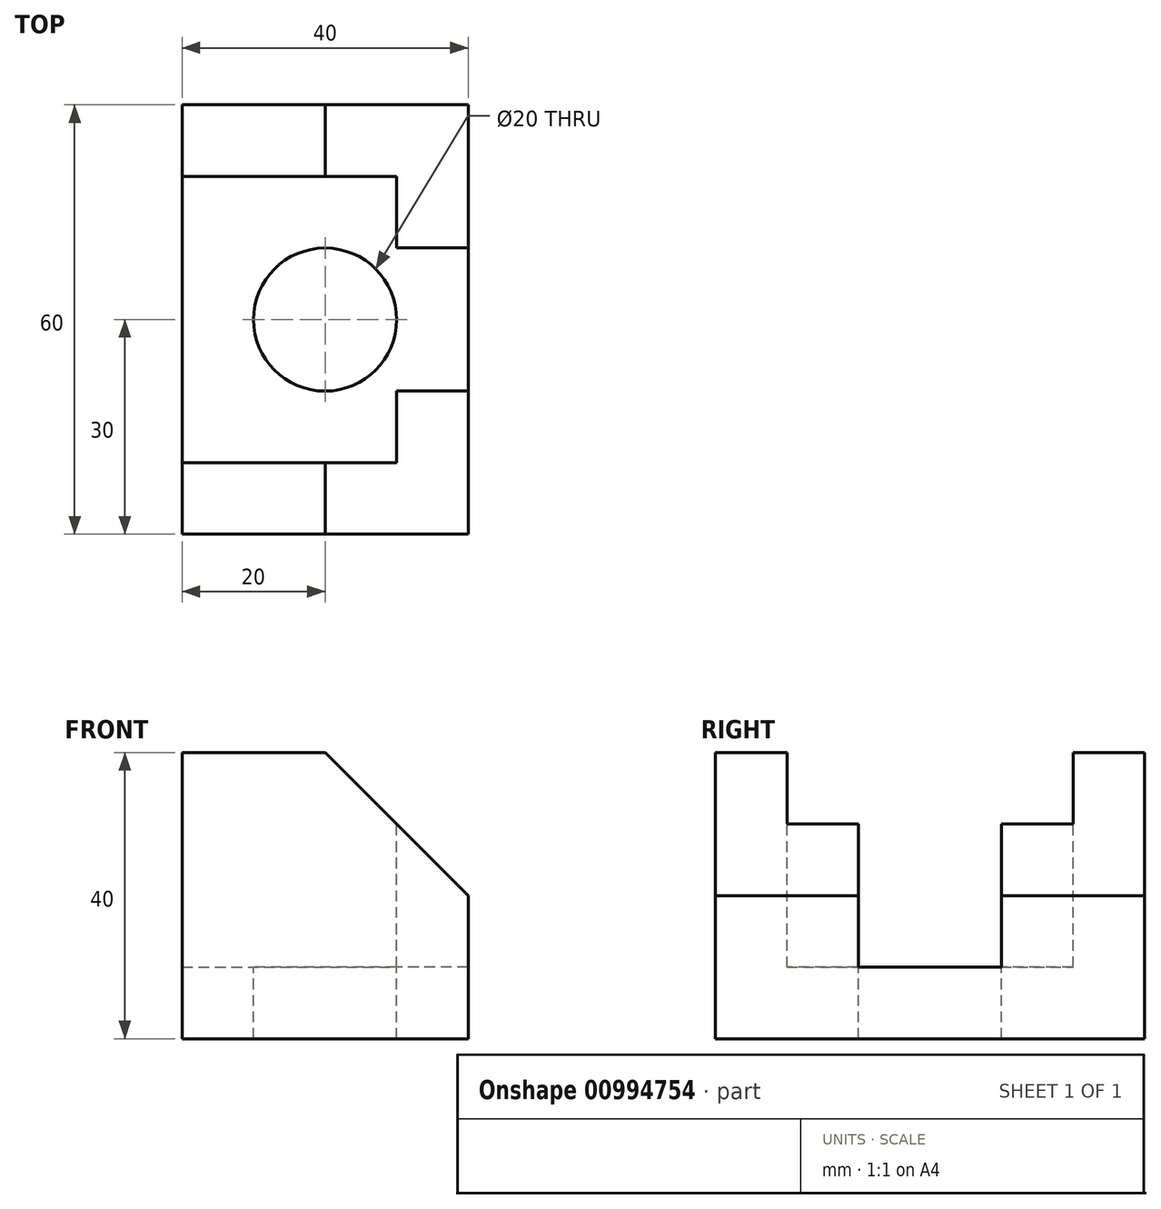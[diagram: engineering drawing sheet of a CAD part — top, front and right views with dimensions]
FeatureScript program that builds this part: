
annotation { "Feature Type Name" : "Feature", "Feature Type Description" : "" }
export const myFeature = defineFeature(function(context is Context, id is Id, definition is map)
    precondition{}
    {
        {
            var Q0;
            Q0=qCreatedBy(makeId("Front.planeOp"),FACE);
            var sketch = newSketch(context, id + "F0", { "sketchPlane" : qUnion([Q0])});
            skLineSegment(sketch, "E0.bottom", {"start": v(-20, 40) * mm, "end": v(0, 40) * mm});
            skLineSegment(sketch, "E0.top", {"start": v(-20, 0) * mm, "end": v(20, 0) * mm});
            skLineSegment(sketch, "E0.left", {"start": v(-20, 40) * mm, "end": v(-20, 0) * mm});
            skLineSegment(sketch, "E0.right", {"start": v(20, 20) * mm, "end": v(20, 0) * mm});
            skLineSegment(sketch, "E1", {"start": v(0, 40) * mm, "end": v(20, 20) * mm});
            skSolve(sketch);
        }
        {
            var Q0;
            Q0 = qSketchRegion(id + "F0", true);
            extrude(context, id + "F1", {"entities" : qUnion([Q0]), "endBound" : BoundingType.SYMMETRIC, "depth" : 60 * mm, "offsetDistance" : 25 * mm});
        }
        {
            var Q0;
            Q0=makeQuery(id+"F1.opExtrude","SWEPT_FACE",FACE,{"disambiguationData":[OSD([sQuery(id+"F0.wireOp",EDGE,"E0.bottom")])]});
            var sketch = newSketch(context, id + "F2", { "sketchPlane" : qUnion([Q0])});
            skLineSegment(sketch, "E2", {"start": v(-20, 20) * mm, "end": v(10, 20) * mm});
            skLineSegment(sketch, "E3", {"start": v(10, 20) * mm, "end": v(10, 10) * mm});
            skLineSegment(sketch, "E4", {"start": v(10, 10) * mm, "end": v(20, 10) * mm});
            skLineSegment(sketch, "E5", {"start": v(20, 10) * mm, "end": v(20, -10) * mm});
            skLineSegment(sketch, "E6", {"start": v(20, -10) * mm, "end": v(10, -10) * mm});
            skLineSegment(sketch, "E7", {"start": v(10, -10) * mm, "end": v(10, -20) * mm});
            skLineSegment(sketch, "E8", {"start": v(10, -20) * mm, "end": v(-20, -20) * mm});
            skLineSegment(sketch, "E9", {"start": v(-20, -20) * mm, "end": v(-20, 20) * mm});
            skSolve(sketch);
        }
        {
            var Q0;
            Q0 = qSketchRegion(id + "F2", true);
            extrude(context, id + "F3", {"entities" : qUnion([Q0]), "operationType" : NewBodyOperationType.REMOVE, "oppositeDirection" : true, "depth" : 30 * mm, "offsetDistance" : 25 * mm});
        }
        {
            var Q0;
            Q0=makeQuery(id+"F3.boolean.opBoolean","COPY",FACE,{"derivedFrom":makeQuery(id+"F3.opExtrude","CAP_FACE",FACE,{"disambiguationData":[OSD([sQuery(id+"F2.wireOp",EDGE,"E2"),sQuery(id+"F2.wireOp",EDGE,"E3"),sQuery(id+"F2.wireOp",EDGE,"E4"),sQuery(id+"F2.wireOp",EDGE,"E5"),sQuery(id+"F2.wireOp",EDGE,"E6"),sQuery(id+"F2.wireOp",EDGE,"E7"),sQuery(id+"F2.wireOp",EDGE,"E8"),sQuery(id+"F2.wireOp",EDGE,"E9")])],"isStart":false})});
            var sketch = newSketch(context, id + "F4", { "sketchPlane" : qUnion([Q0])});
            skCircle(sketch, "E10", {"center": v(0, 0) * mm, "radius": 10 * mm});
            skSolve(sketch);
        }
        {
            var Q0;
            Q0 = qSketchRegion(id + "F4", true);
            extrude(context, id + "F5", {"entities" : qUnion([Q0]), "operationType" : NewBodyOperationType.REMOVE, "oppositeDirection" : true, "depth" : 25 * mm, "offsetDistance" : 25 * mm});
        }
    });
